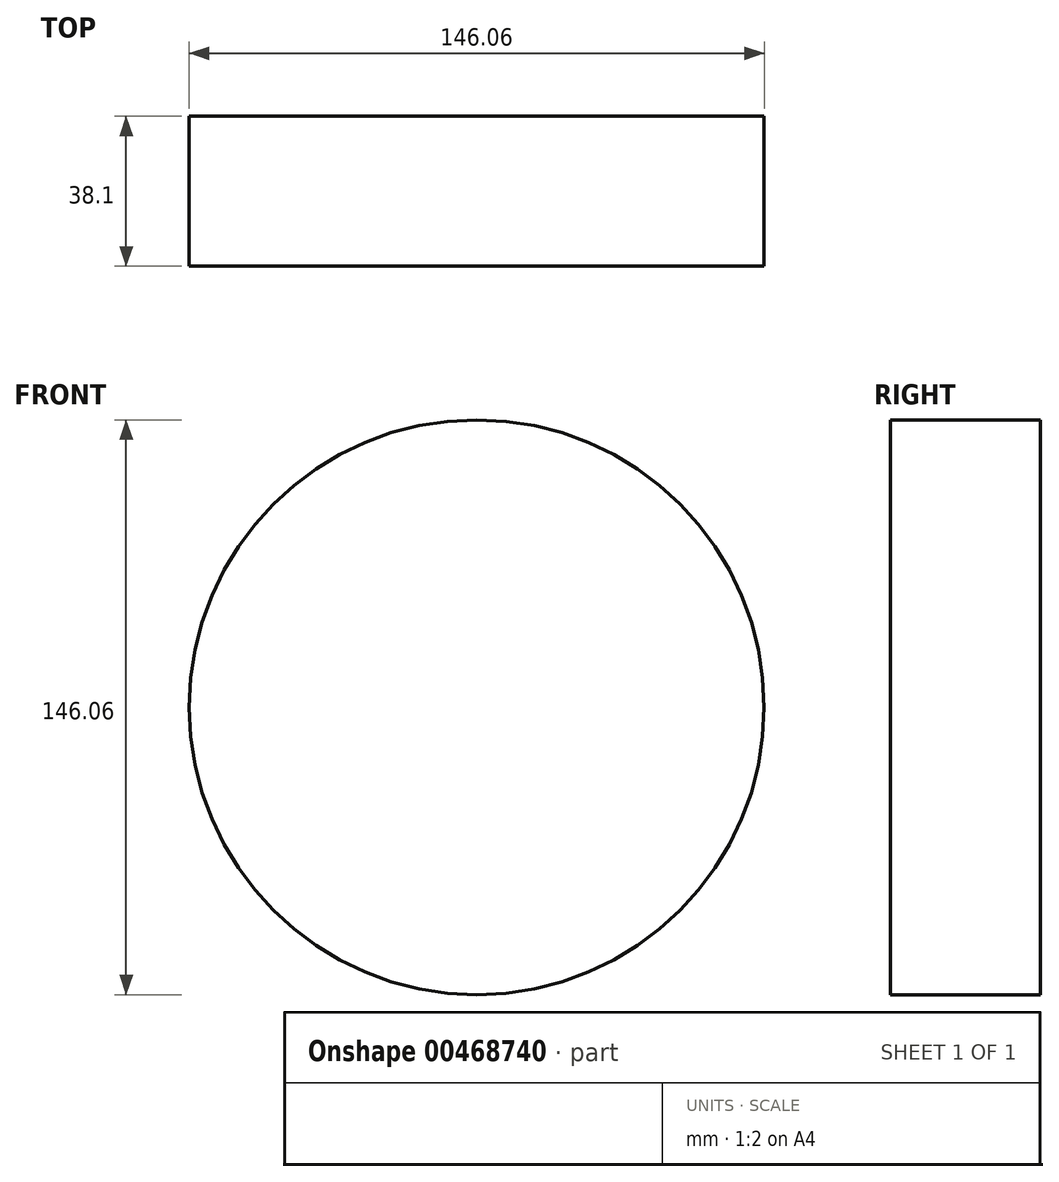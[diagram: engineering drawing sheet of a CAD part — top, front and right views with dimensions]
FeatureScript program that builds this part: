
annotation { "Feature Type Name" : "Feature", "Feature Type Description" : "" }
export const myFeature = defineFeature(function(context is Context, id is Id, definition is map)
    precondition{}
    {
        {
            var Q0;
            Q0=qCreatedBy(makeId("Front.planeOp"),FACE);
            var sketch = newSketch(context, id + "F0", { "sketchPlane" : qUnion([Q0])});
            skCircle(sketch, "E0", {"center": v(-129.54, 0) * mm, "radius": 73.03 * mm});
            skLineSegment(sketch, "E1", {"start": v(447.04, -320.04) * mm, "end": v(-447.04, -320.04) * mm});
            skLineSegment(sketch, "E2", {"start": v(-447.04, -320.04) * mm, "end": v(-447.04, 320.04) * mm});
            skCircle(sketch, "E3", {"center": v(-338, 211) * mm, "radius": 61.34 * mm});
            skCircle(sketch, "E4", {"center": v(338, 211) * mm, "radius": 61.34 * mm});
            skCircle(sketch, "E5", {"center": v(338, -211) * mm, "radius": 61.34 * mm});
            skCircle(sketch, "E6", {"center": v(-338.19, -210.81) * mm, "radius": 61.34 * mm});
            skLineSegment(sketch, "E7", {"start": v(-447.04, 320.04) * mm, "end": v(447.04, 320.04) * mm});
            skLineSegment(sketch, "E8", {"start": v(447.04, 320.04) * mm, "end": v(447.04, -320.04) * mm});
            skSolve(sketch);
        }
        {
            var Q0;
            Q0=makeQuery(id+"F0.imprint","IMPRINT",FACE,{"disambiguationData":[TD([[makeQuery(id+"F0.imprint","IMPRINT",EDGE,{"derivedFrom":sQuery(id+"F0.wireOp",EDGE,"E0")}),1.0]])]});
            extrude(context, id + "F1", {"entities" : qUnion([Q0]), "depth" : 38.1 * mm});
        }
    });
